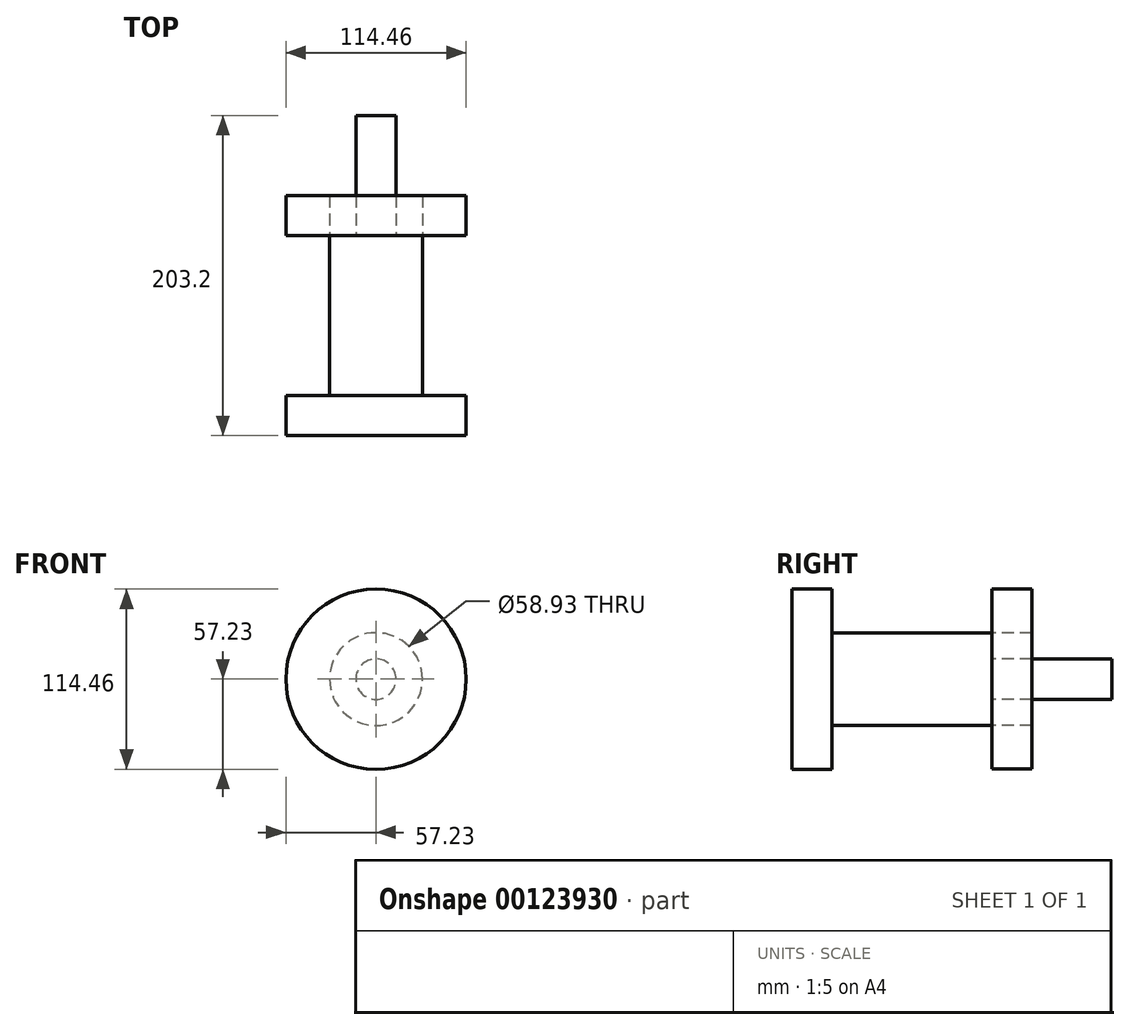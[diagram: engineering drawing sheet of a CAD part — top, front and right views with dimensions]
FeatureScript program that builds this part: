
annotation { "Feature Type Name" : "Feature", "Feature Type Description" : "" }
export const myFeature = defineFeature(function(context is Context, id is Id, definition is map)
    precondition{}
    {
        {
            var Q0;
            Q0=qCreatedBy(makeId("Front.planeOp"),FACE);
            var sketch = newSketch(context, id + "F0", { "sketchPlane" : qUnion([Q0])});
            skCircle(sketch, "E0", {"center": v(0, 0) * mm, "radius": 57.23 * mm});
            skCircle(sketch, "E1", {"center": v(0, 0) * mm, "radius": 21.32 * mm});
            skSolve(sketch);
        }
        {
            var Q0;
            Q0=makeQuery(id+"F0.imprint","IMPRINT",FACE,{"disambiguationData":[TD([[makeQuery(id+"F0.imprint","IMPRINT",EDGE,{"derivedFrom":sQuery(id+"F0.wireOp",EDGE,"E0")}),1.0]])]});
            var Q1;
            Q1=makeQuery(id+"F0.imprint","IMPRINT",FACE,{"disambiguationData":[TD([[makeQuery(id+"F0.imprint","IMPRINT",EDGE,{"derivedFrom":sQuery(id+"F0.wireOp",EDGE,"E1")}),1.0]])]});
            extrude(context, id + "F1", {"entities" : qUnion([Q0, Q1]), "oppositeDirection" : true, "depth" : 25.4 * mm});
        }
        {
            var Q0;
            Q0=qCreatedBy(makeId("Front.planeOp"),FACE);
            var sketch = newSketch(context, id + "F2", { "sketchPlane" : qUnion([Q0])});
            skCircle(sketch, "E2", {"center": v(0, 0) * mm, "radius": 29.46 * mm});
            skSolve(sketch);
        }
        {
            var Q0;
            Q0=makeQuery(id+"F2.imprint","IMPRINT",FACE,{"disambiguationData":[TD([[makeQuery(id+"F2.imprint","IMPRINT",EDGE,{"derivedFrom":sQuery(id+"F2.wireOp",EDGE,"E2")}),1.0]])]});
            extrude(context, id + "F3", {"entities" : qUnion([Q0]), "operationType" : NewBodyOperationType.ADD, "oppositeDirection" : true, "depth" : 127 * mm});
        }
        {
            var Q0;
            Q0=makeQuery(id+"F3.opExtrude","CAP_FACE",FACE,{"disambiguationData":[OSD([sQuery(id+"F2.wireOp",EDGE,"E2")])],"isStart":false});
            var sketch = newSketch(context, id + "F4", { "sketchPlane" : qUnion([Q0])});
            skCircle(sketch, "E3", {"center": v(0, 0) * mm, "radius": 57.15 * mm});
            skSolve(sketch);
        }
        {
            var Q0;
            Q0=makeQuery(id+"F4.imprint","IMPRINT",FACE,{"disambiguationData":[TD([[makeQuery(id+"F4.imprint","IMPRINT",EDGE,{"derivedFrom":sQuery(id+"F4.wireOp",EDGE,"E3")}),1.0]])]});
            extrude(context, id + "F5", {"entities" : qUnion([Q0]), "depth" : 25.4 * mm});
        }
        {
            var Q0;
            Q0=makeQuery(id+"F3.opExtrude","CAP_FACE",FACE,{"disambiguationData":[OSD([sQuery(id+"F2.wireOp",EDGE,"E2")])],"isStart":false});
            var sketch = newSketch(context, id + "F6", { "sketchPlane" : qUnion([Q0])});
            skCircle(sketch, "E4", {"center": v(0, 0) * mm, "radius": 12.79 * mm});
            skSolve(sketch);
        }
        {
            var Q0;
            Q0=makeQuery(id+"F6.imprint","IMPRINT",FACE,{"disambiguationData":[TD([[makeQuery(id+"F6.imprint","IMPRINT",EDGE,{"derivedFrom":sQuery(id+"F6.wireOp",EDGE,"E4")}),1.0]])]});
            extrude(context, id + "F7", {"entities" : qUnion([Q0]), "operationType" : NewBodyOperationType.ADD, "depth" : 76.2 * mm});
        }
    });
